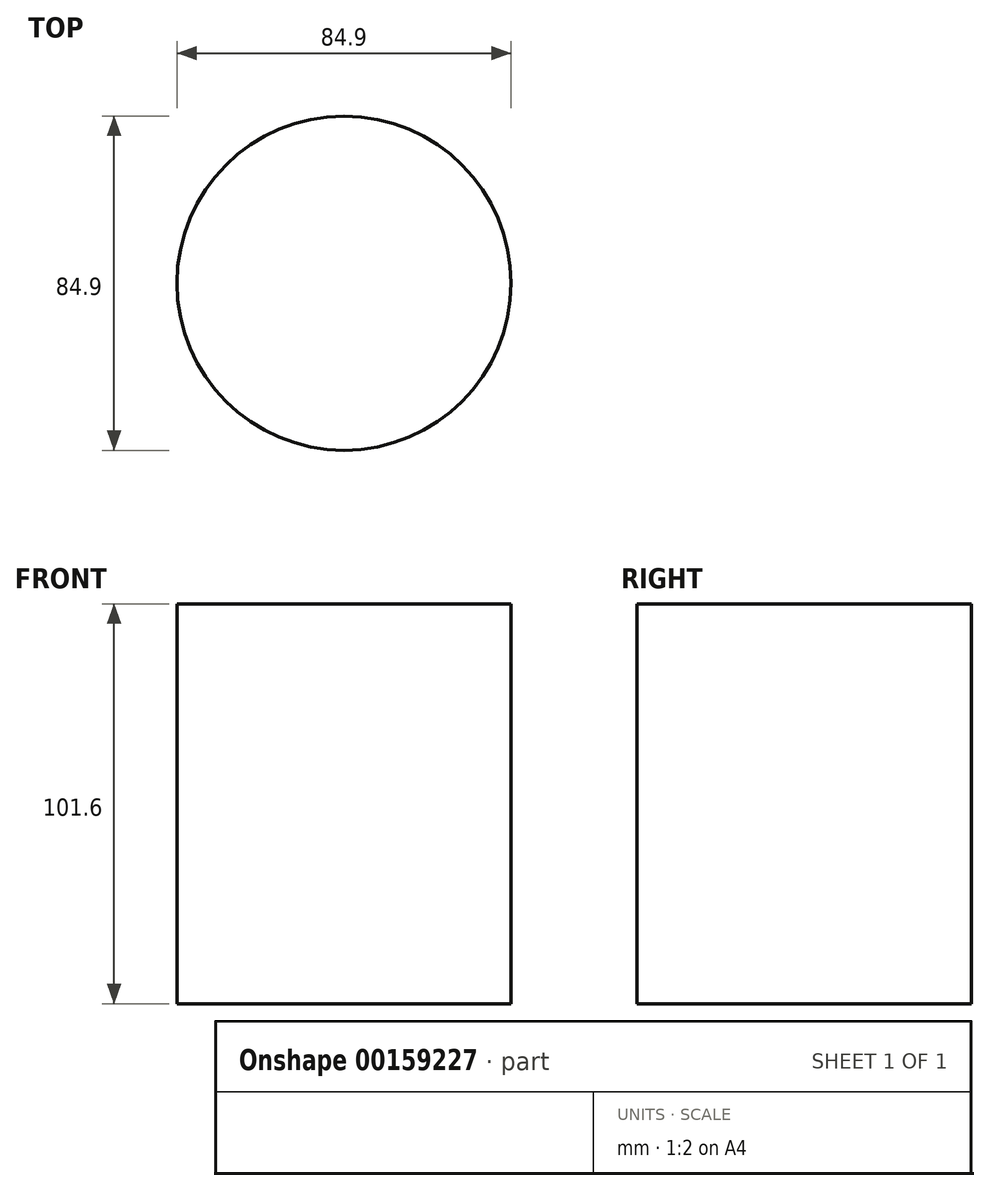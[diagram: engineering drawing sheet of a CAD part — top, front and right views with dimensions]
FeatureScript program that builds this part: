
annotation { "Feature Type Name" : "Feature", "Feature Type Description" : "" }
export const myFeature = defineFeature(function(context is Context, id is Id, definition is map)
    precondition{}
    {
        {
            var Q0;
            Q0=qCreatedBy(makeId("Top.planeOp"),FACE);
            var sketch = newSketch(context, id + "F0", { "sketchPlane" : qUnion([Q0])});
            skCircle(sketch, "E0", {"center": v(0, 0) * mm, "radius": 42.45 * mm});
            skSolve(sketch);
        }
        {
            var Q0;
            Q0=makeQuery(id+"F0.imprint","IMPRINT",FACE,{"disambiguationData":[TD([[makeQuery(id+"F0.imprint","IMPRINT",EDGE,{"derivedFrom":sQuery(id+"F0.wireOp",EDGE,"E0")}),1.0]])]});
            extrude(context, id + "F1", {"entities" : qUnion([Q0]), "depth" : 101.6 * mm});
        }
    });
